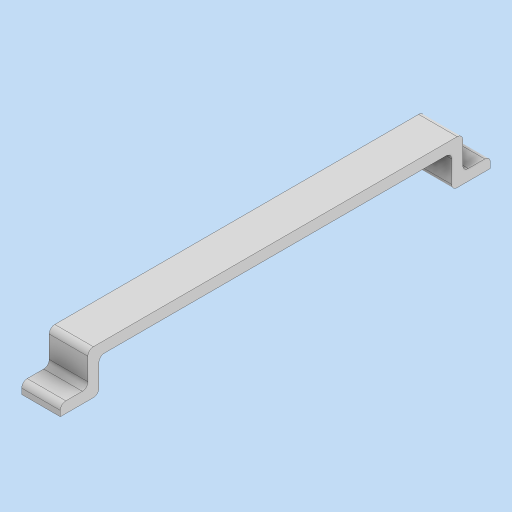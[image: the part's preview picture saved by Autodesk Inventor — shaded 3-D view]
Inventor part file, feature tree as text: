
AUTODESK INVENTOR PART (.ipt)
format: ipt  version: 2024 (Build 280153000, 153)  size: 150,528 bytes
history: native  units: mm
features: extrude x3, sketch x3, fillet x2
ambient origin geometry x8: Origin, YZ Plane, XZ Plane, XY Plane, X Axis, Y Axis, Z Axis, Center Point
bodies: Solid1 (feature_tree)
feature tree (8):
  extrude  "Extrusion1"  Depth=7.0mm
  extrude  "Extrusion2"  Depth=2.0mm
  extrude  "Extrusion3"  Depth=4.0mm TaperAngle=0.0deg
  fillet  "Fillet3"  Radius=2.0mm
  fillet  "Fillet4"  Radius=1.0mm
  sketch  "Sketch1"  dims[d0=78.0mm d1=7.0mm]
  sketch  "Sketch2"  dims[d2=2.0mm d3=0.0mm d4=2.0mm]
  sketch  "Sketch3"  dims[d5=2.0mm d6=4.0mm d7=0.0mm d10=2.0mm d11=0.0mm d12=1.0mm d13=1.0mm]
